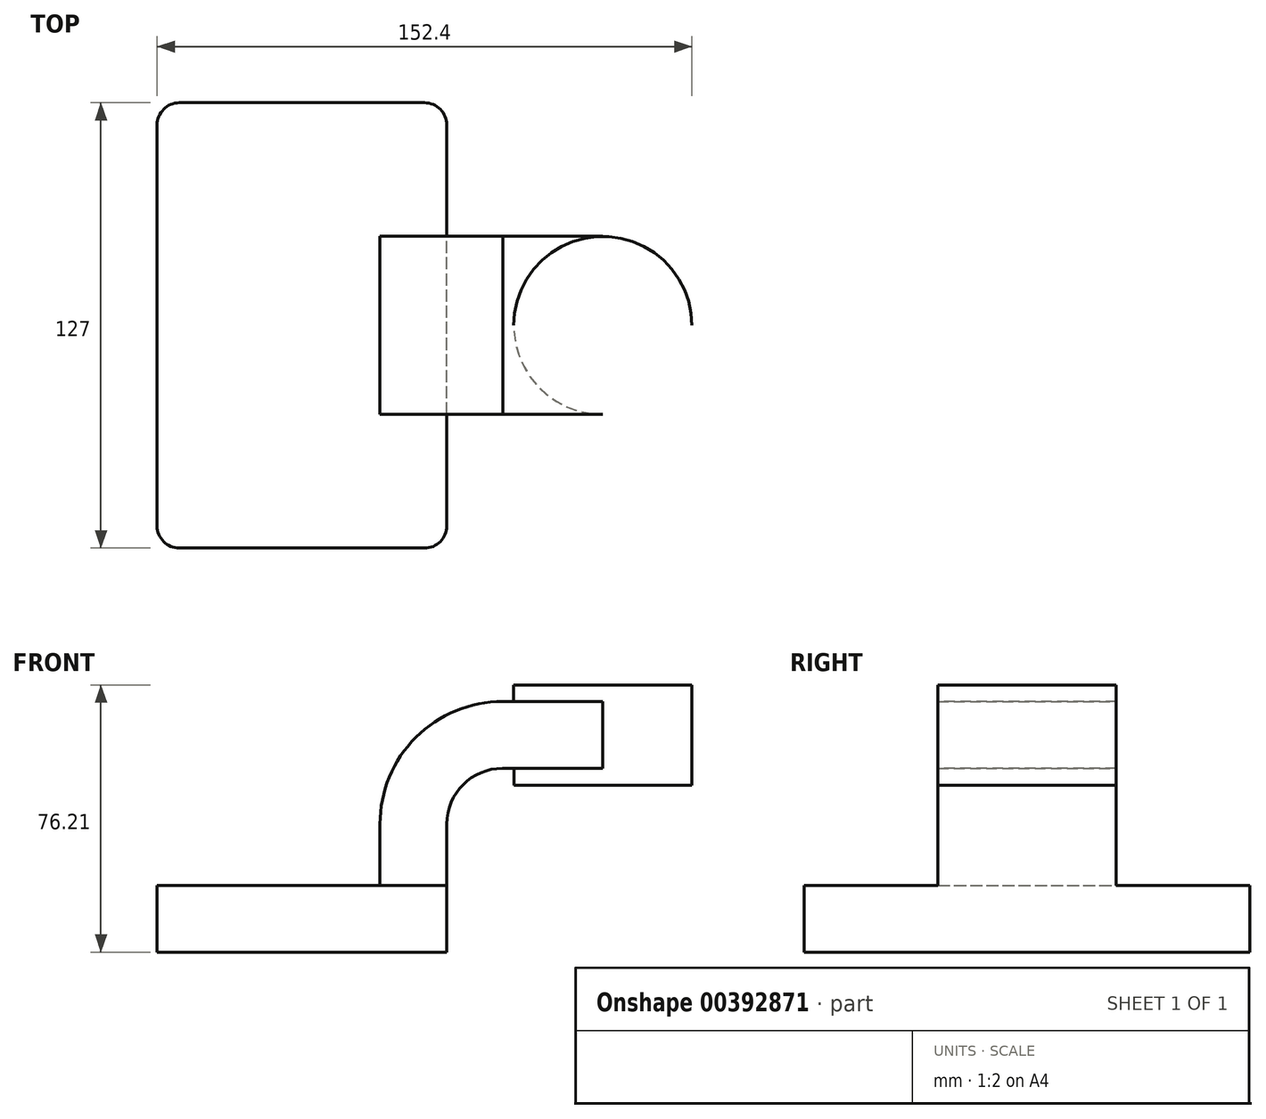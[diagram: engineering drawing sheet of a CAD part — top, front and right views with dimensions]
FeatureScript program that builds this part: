
annotation { "Feature Type Name" : "Feature", "Feature Type Description" : "" }
export const myFeature = defineFeature(function(context is Context, id is Id, definition is map)
    precondition{}
    {
        {
            var Q0;
            Q0=qCreatedBy(makeId("Front.planeOp"),FACE);
            var sketch = newSketch(context, id + "F0", { "sketchPlane" : qUnion([Q0])});
            skLineSegment(sketch, "E0.bottom", {"start": v(-41.28, -9.53) * mm, "end": v(41.28, -9.53) * mm});
            skLineSegment(sketch, "E0.top", {"start": v(-41.28, 9.53) * mm, "end": v(41.28, 9.53) * mm});
            skLineSegment(sketch, "E0.left", {"start": v(-41.28, -9.53) * mm, "end": v(-41.28, 9.53) * mm});
            skLineSegment(sketch, "E0.right", {"start": v(41.28, -9.53) * mm, "end": v(41.28, 9.53) * mm});
            skPoint(sketch, "E0.middle", {"position": v(0, 0) * mm});
            skLineSegment(sketch, "E1.bottom", {"start": v(60.32, 38.1) * mm, "end": v(111.12, 38.1) * mm});
            skLineSegment(sketch, "E1.top", {"start": v(60.32, 66.67) * mm, "end": v(111.12, 66.67) * mm});
            skLineSegment(sketch, "E1.left", {"start": v(60.32, 38.1) * mm, "end": v(60.32, 66.67) * mm});
            skLineSegment(sketch, "E1.right", {"start": v(111.12, 38.1) * mm, "end": v(111.12, 66.67) * mm});
            skPoint(sketch, "E1.middle", {"position": v(85.72, 52.39) * mm});
            skLineSegment(sketch, "E2", {"start": v(41.27, 9.53) * mm, "end": v(41.27, 27) * mm});
            skArc(sketch, "E3", {"start": v(41.27, 27) * mm, "mid": v(45.92, 38.23) * mm, "end": v(57.15, 42.88) * mm});
            skLineSegment(sketch, "E4", {"start": v(57.15, 42.88) * mm, "end": v(85.76, 42.88) * mm});
            skArc(sketch, "E5.1", {"start": v(22.22, 27) * mm, "mid": v(32.47, 51.71) * mm, "end": v(57.2, 61.93) * mm});
            skLineSegment(sketch, "E5.2", {"start": v(22.22, 9.53) * mm, "end": v(22.22, 27) * mm});
            skLineSegment(sketch, "E6.0", {"start": v(57.15, 61.93) * mm, "end": v(85.76, 61.93) * mm});
            skLineSegment(sketch, "E7", {"start": v(85.72, 66.67) * mm, "end": v(85.76, 38.1) * mm});
            skFitSpline(sketch, "E8", {"points": [v(-41.28, 9.53) * mm, v(57.2, 61.93) * mm], "startDerivative": vector(3.6, 106.42) * mm, "endDerivative": vector(114.62, -0.37) * mm});
            skSolve(sketch);
        }
        {
            var Q0;
            Q0=makeQuery(id+"F0.imprint","IMPRINT",FACE,{"disambiguationData":[TD([[makeQuery(id+"F0.imprint","IMPRINT",EDGE,{"derivedFrom":sQuery(id+"F0.wireOp",EDGE,"E0.bottom")}),1.0]])]});
            extrude(context, id + "F1", {"entities" : qUnion([Q0]), "endBound" : BoundingType.SYMMETRIC, "depth" : 127 * mm});
        }
        {
            var Q0;
            {var subQ1=sQuery(id+"F0.wireOp",EDGE,"E2");Q0=makeQuery(id+"F0.imprint","IMPRINT",FACE,{"disambiguationData":[TD([[makeQuery(id+"F0.imprint","IMPRINT",EDGE,{"derivedFrom":subQ1}),1.0]])]});}
            var Q1;
            {var subQ0=sQuery(id+"F0.wireOp",EDGE,"E4");var subQ1=sQuery(id+"F0.wireOp",EDGE,"E1.left");var subQ2=makeQuery(id+"F0.imprint","INTERSECT",VERTEX,{"derivedFrom":[subQ1,subQ0]});Q1=makeQuery(id+"F0.imprint","IMPRINT",FACE,{"disambiguationData":[TD([[makeQuery(id+"F0.imprint","IMPRINT",EDGE,{"disambiguationData":[TD([[subQ2,-1.0]])],"derivedFrom":subQ1}),-1.0]])]});}
            extrude(context, id + "F2", {"entities" : qUnion([Q0, Q1]), "operationType" : NewBodyOperationType.ADD, "endBound" : BoundingType.SYMMETRIC, "depth" : 50.8 * mm});
        }
        {
            var Q0;
            {var subQ4=sQuery(id+"F0.wireOp",EDGE,"E5.1");Q0=makeQuery(id+"F0.imprint","IMPRINT",FACE,{"disambiguationData":[TD([[makeQuery(id+"F0.imprint","IMPRINT",EDGE,{"derivedFrom":subQ4}),1.0]])]});}
            extrude(context, id + "F3", {"entities" : qUnion([Q0]), "operationType" : NewBodyOperationType.ADD, "endBound" : BoundingType.SYMMETRIC, "depth" : 15.88 * mm});
        }
        {
            var Q0;
            {var subQ0=sQuery(id+"F0.wireOp",EDGE,"E1.right");Q0=makeQuery(id+"F0.imprint","IMPRINT",FACE,{"disambiguationData":[TD([[makeQuery(id+"F0.imprint","IMPRINT",EDGE,{"derivedFrom":subQ0}),1.0]])]});}
            var Q1;
            Q1=sQuery(id+"F0.wireOp",EDGE,"E7");
            revolve(context, id + "F4", {"operationType" : NewBodyOperationType.ADD, "entities" : qUnion([Q0]), "axis" : qUnion([Q1]), "revolveType" : RevolveType.FULL});
        }
        {
            var Q0;
            Q0=makeQuery(id+"F1.opExtrude","CAP_EDGE",EDGE,{"disambiguationData":[OSD([sQuery(id+"F0.wireOp",EDGE,"E0.right")])],"isStart":false});
            var Q1;
            Q1=makeQuery(id+"F1.opExtrude","CAP_EDGE",EDGE,{"disambiguationData":[OSD([sQuery(id+"F0.wireOp",EDGE,"E0.right")])],"isStart":true});
            var Q2;
            Q2=makeQuery(id+"F1.opExtrude","CAP_EDGE",EDGE,{"disambiguationData":[OSD([sQuery(id+"F0.wireOp",EDGE,"E0.left")])],"isStart":false});
            var Q3;
            Q3=makeQuery(id+"F1.opExtrude","CAP_EDGE",EDGE,{"disambiguationData":[OSD([sQuery(id+"F0.wireOp",EDGE,"E0.left")])],"isStart":true});
            fillet(context, id + "F5", {"entities" : qUnion([Q0, Q1, Q2, Q3]), "radius" : 6.35 * mm, "tangentPropagation" : true, "allowEdgeOverflow" : false});
        }
    });
